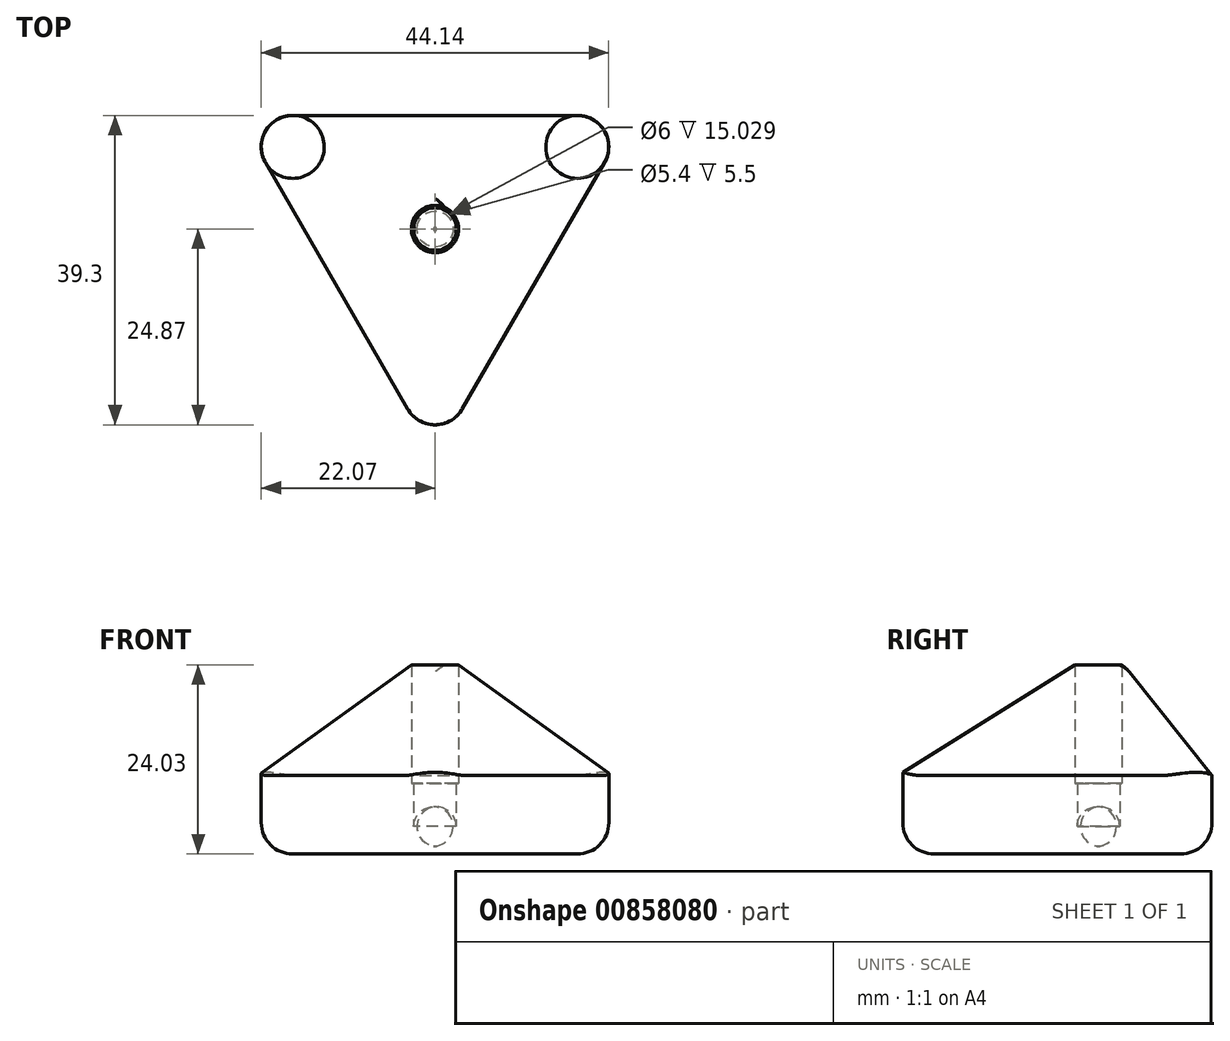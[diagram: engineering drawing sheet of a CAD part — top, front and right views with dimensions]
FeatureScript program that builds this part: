
annotation { "Feature Type Name" : "Feature", "Feature Type Description" : "" }
export const myFeature = defineFeature(function(context is Context, id is Id, definition is map)
    precondition{}
    {
        {
            var Q0;
            Q0=qCreatedBy(makeId("Top.planeOp"),FACE);
            var sketch = newSketch(context, id + "F0", { "sketchPlane" : qUnion([Q0])});
            skCircle(sketch, "E0.cCircle", {"center": v(0, 0) * mm, "radius": 14.43 * mm, "construction": true});
            skLineSegment(sketch, "E0.0", {"start": v(-25, 14.43) * mm, "end": v(25, 14.43) * mm});
            skLineSegment(sketch, "E0.1", {"start": v(25, 14.43) * mm, "end": v(0, -28.87) * mm});
            skLineSegment(sketch, "E0.2", {"start": v(0, -28.87) * mm, "end": v(-25, 14.43) * mm});
            skPoint(sketch, "E0.0.midPoint", {"position": v(0, 14.43) * mm});
            skSolve(sketch);
        }
        {
            var Q0;
            Q0=qCreatedBy(makeId("Top.planeOp"),FACE);
            cPlane(context, id + "F1", {"entities" : qUnion([Q0]), "cplaneType" : CPlaneType.OFFSET, "offset" : 18 * mm, "width" : 150 * mm, "height" : 150 * mm});
        }
        {
            var Q0;
            Q0=qCreatedBy(id+"F1.planeOp",FACE);
            var sketch = newSketch(context, id + "F2", { "sketchPlane" : qUnion([Q0])});
            skPoint(sketch, "E1", {"position": v(0, 0) * mm});
            skSolve(sketch);
        }
        {
            var Q0;
            Q0=makeQuery(id+"F0.imprint","IMPRINT",FACE,{"disambiguationData":[TD([[makeQuery(id+"F0.imprint","IMPRINT",EDGE,{"derivedFrom":sQuery(id+"F0.wireOp",EDGE,"E0.0")}),-1.0]])]});
            var Q1;
            Q1=sQuery(id+"F2.wireOp",VERTEX,"E1");
            loft(context, id + "F3", {"sheetProfilesArray" : [{ "sheetProfileEntities" : qUnion([Q0]) }, { "sheetProfileEntities" : qUnion([Q1]) }]});
        }
        {
            var Q0;
            Q0=makeQuery(id+"F3.opLoft","SWEPT_EDGE",EDGE,{"disambiguationData":[OSD([sQuery(id+"F0.wireOp",EDGE,"E0.1"),sQuery(id+"F0.wireOp",EDGE,"E0.2"),sQuery(id+"F2.wireOp",VERTEX,"E1")])]});
            var Q1;
            Q1=makeQuery(id+"F3.opLoft","SWEPT_EDGE",EDGE,{"disambiguationData":[OSD([sQuery(id+"F0.wireOp",EDGE,"E0.0"),sQuery(id+"F0.wireOp",EDGE,"E0.2"),sQuery(id+"F2.wireOp",VERTEX,"E1")])]});
            var Q2;
            Q2=makeQuery(id+"F3.opLoft","SWEPT_EDGE",EDGE,{"disambiguationData":[OSD([sQuery(id+"F0.wireOp",EDGE,"E0.0"),sQuery(id+"F0.wireOp",EDGE,"E0.1"),sQuery(id+"F2.wireOp",VERTEX,"E1")])]});
            fillet(context, id + "F4", {"entities" : qUnion([Q0, Q1, Q2]), "radius" : 5 * mm, "tangentPropagation" : true, "allowEdgeOverflow" : false});
        }
        {
            var Q0;
            Q0=qCreatedBy(makeId("Top.planeOp"),FACE);
            cPlane(context, id + "F5", {"entities" : qUnion([Q0]), "cplaneType" : CPlaneType.OFFSET, "offset" : 9 * mm, "oppositeDirection" : true, "width" : 150 * mm, "height" : 150 * mm});
        }
        {
            var Q0;
            Q0=qCreatedBy(id+"F5.planeOp",FACE);
            var sketch = newSketch(context, id + "F6", { "sketchPlane" : qUnion([Q0])});
            skCircle(sketch, "E2", {"center": v(0, 0) * mm, "radius": 2.7 * mm});
            skSolve(sketch);
        }
        {
            var Q0;
            Q0=qCreatedBy(id+"F5.planeOp",FACE);
            cPlane(context, id + "F7", {"entities" : qUnion([Q0]), "cplaneType" : CPlaneType.OFFSET, "offset" : 8 * mm, "width" : 150 * mm, "height" : 150 * mm});
        }
        {
            var Q0;
            Q0=qCreatedBy(id+"F7.planeOp",FACE);
            var sketch = newSketch(context, id + "F8", { "sketchPlane" : qUnion([Q0])});
            skCircle(sketch, "E3", {"center": v(0, 0) * mm, "radius": 3 * mm});
            skSolve(sketch);
        }
        {
            var Q0;
            Q0 = qSketchRegion(id + "F0", true);
            extrude(context, id + "F9", {"entities" : qUnion([Q0]), "operationType" : NewBodyOperationType.ADD, "oppositeDirection" : true, "depth" : 10 * mm, "offsetDistance" : 25 * mm});
        }
        {
            var Q0;
            Q0=makeQuery(id+"F9.opExtrude","SWEPT_EDGE",EDGE,{"disambiguationData":[OSD([sQuery(id+"F0.wireOp",EDGE,"E0.0"),sQuery(id+"F0.wireOp",EDGE,"E0.1")])]});
            var Q1;
            Q1=makeQuery(id+"F9.opExtrude","SWEPT_EDGE",EDGE,{"disambiguationData":[OSD([sQuery(id+"F0.wireOp",EDGE,"E0.0"),sQuery(id+"F0.wireOp",EDGE,"E0.2")])]});
            var Q2;
            Q2=makeQuery(id+"F9.opExtrude","SWEPT_EDGE",EDGE,{"disambiguationData":[OSD([sQuery(id+"F0.wireOp",EDGE,"E0.1"),sQuery(id+"F0.wireOp",EDGE,"E0.2")])]});
            var Q3;
            Q3=makeQuery(id+"F9.opExtrude","CAP_EDGE",EDGE,{"disambiguationData":[OSD([sQuery(id+"F0.wireOp",EDGE,"E0.0")])],"isStart":false});
            var Q4;
            Q4=makeQuery(id+"F9.opExtrude","CAP_EDGE",EDGE,{"disambiguationData":[OSD([sQuery(id+"F0.wireOp",EDGE,"E0.2")])],"isStart":false});
            var Q5;
            Q5=makeQuery(id+"F9.opExtrude","CAP_FACE",FACE,{"disambiguationData":[OSD([sQuery(id+"F0.wireOp",EDGE,"E0.0"),sQuery(id+"F0.wireOp",EDGE,"E0.1"),sQuery(id+"F0.wireOp",EDGE,"E0.2")])],"isStart":false});
            fillet(context, id + "F10", {"entities" : qUnion([Q0, Q1, Q2, Q3, Q4, Q5]), "radius" : 4 * mm, "tangentPropagation" : true, "allowEdgeOverflow" : false});
        }
        {
            var Q0;
            Q0 = qSketchRegion(id + "F6", true);
            extrude(context, id + "F11", {"entities" : qUnion([Q0]), "operationType" : NewBodyOperationType.REMOVE, "depth" : 8 * mm, "offsetDistance" : 25 * mm});
        }
        {
            var Q0;
            Q0 = qSketchRegion(id + "F8", true);
            extrude(context, id + "F12", {"entities" : qUnion([Q0]), "operationType" : NewBodyOperationType.REMOVE, "depth" : 25 * mm, "offsetDistance" : 25 * mm});
        }
        {
            var Q0;
            Q0=makeQuery(id+"F11.boolean.opBoolean","COPY",EDGE,{"derivedFrom":makeQuery(id+"F11.opExtrude","CAP_EDGE",EDGE,{"disambiguationData":[OSD([sQuery(id+"F6.wireOp",EDGE,"E2")])],"isStart":true})});
            fillet(context, id + "F13", {"entities" : qUnion([Q0]), "radius" : 2.5 * mm, "tangentPropagation" : true, "allowEdgeOverflow" : false});
        }
    });
